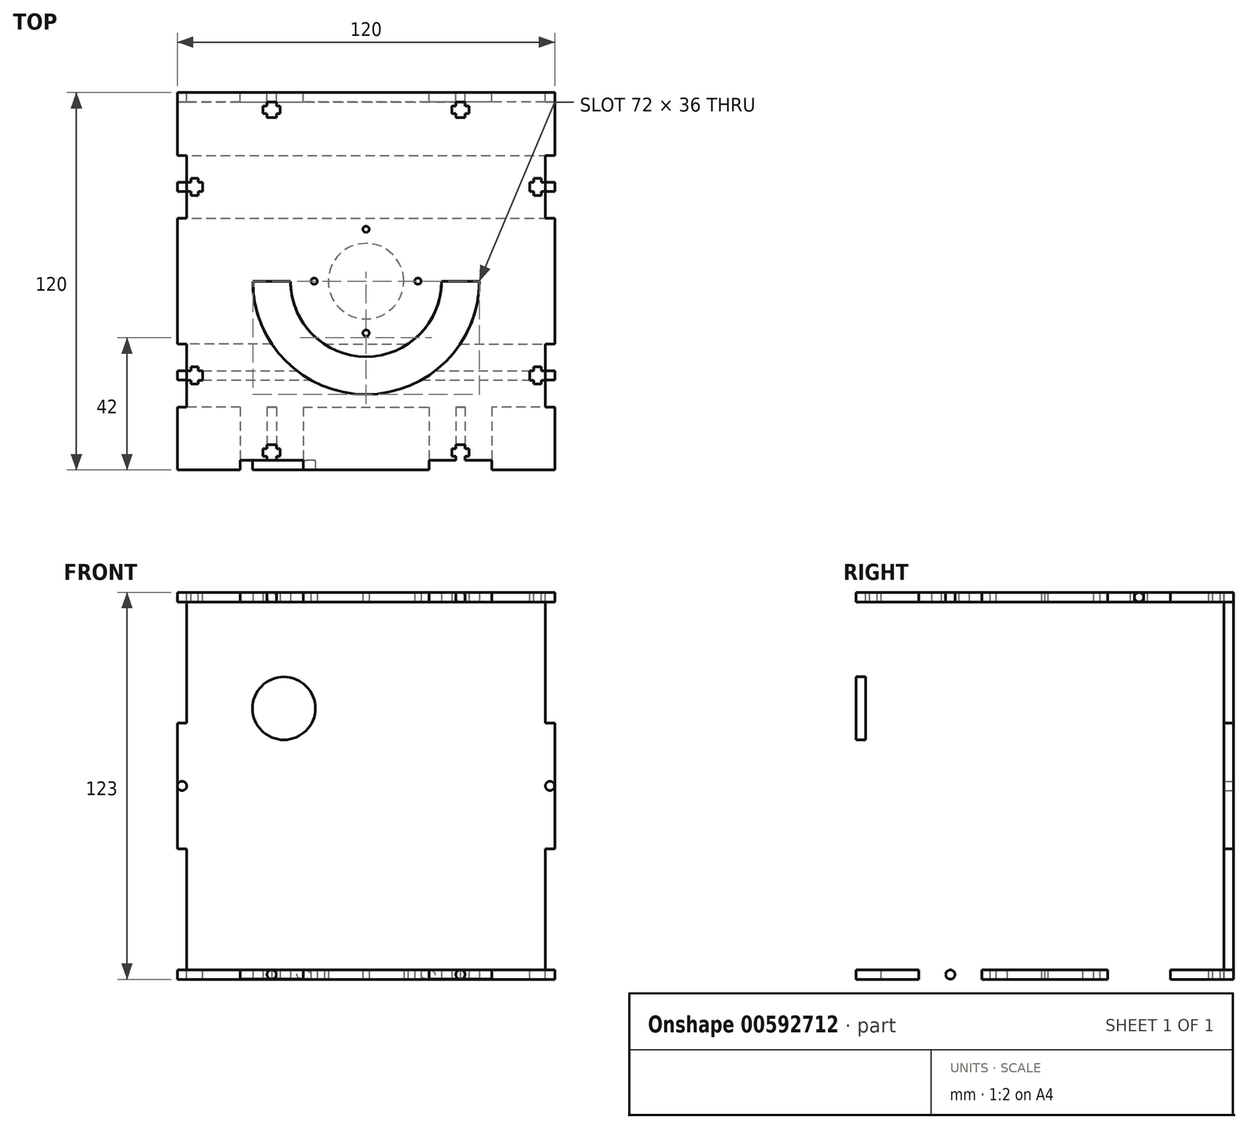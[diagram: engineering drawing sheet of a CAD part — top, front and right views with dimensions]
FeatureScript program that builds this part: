
annotation { "Feature Type Name" : "Feature", "Feature Type Description" : "" }
export const myFeature = defineFeature(function(context is Context, id is Id, definition is map)
    precondition{}
    {
        {
            var Q0;
            Q0=qCreatedBy(makeId("Top.planeOp"),FACE);
            var sketch = newSketch(context, id + "F0", { "sketchPlane" : qUnion([Q0])});
            skLineSegment(sketch, "E0.bottom", {"start": v(-60, 60) * mm, "end": v(-40, 60) * mm});
            skLineSegment(sketch, "E0.top", {"start": v(-60, -60) * mm, "end": v(-40, -60) * mm});
            skLineSegment(sketch, "E0.left", {"start": v(-60, 60) * mm, "end": v(-60, 40) * mm});
            skLineSegment(sketch, "E0.right", {"start": v(60, 60) * mm, "end": v(60, 40) * mm});
            skCircle(sketch, "E1", {"center": v(0, 0) * mm, "radius": 12 * mm});
            skCircle(sketch, "E2", {"center": v(0, -16.5) * mm, "radius": 1 * mm});
            skCircle(sketch, "E3.MirrorC", {"center": v(0, 16.5) * mm, "radius": 1 * mm});
            skLineSegment(sketch, "E4", {"start": v(57, -70.63) * mm, "end": v(57, -31.5) * mm, "construction": true});
            skLineSegment(sketch, "E5", {"start": v(-40, -57) * mm, "end": v(-40, -60) * mm});
            skLineSegment(sketch, "E6", {"start": v(-20, -57) * mm, "end": v(-20, -60) * mm});
            skLineSegment(sketch, "E7.trimOffspring", {"start": v(-20, -60) * mm, "end": v(20, -60) * mm});
            skLineSegment(sketch, "E8", {"start": v(-40, -57) * mm, "end": v(-31.5, -57) * mm});
            skLineSegment(sketch, "E9.bottom", {"start": v(-32.75, -53.3) * mm, "end": v(-31.5, -53.3) * mm});
            skLineSegment(sketch, "E9.top", {"start": v(-32.75, -55.7) * mm, "end": v(-31.5, -55.7) * mm});
            skLineSegment(sketch, "E9.left", {"start": v(-32.75, -53.3) * mm, "end": v(-32.75, -55.7) * mm});
            skLineSegment(sketch, "E9.right", {"start": v(-27.25, -53.3) * mm, "end": v(-27.25, -55.7) * mm});
            skPoint(sketch, "E9.middle", {"position": v(-30, -54.5) * mm});
            skLineSegment(sketch, "E10.top", {"start": v(-28.5, -52) * mm, "end": v(-31.5, -52) * mm});
            skLineSegment(sketch, "E10.left", {"start": v(-28.5, -57) * mm, "end": v(-28.5, -55.7) * mm});
            skLineSegment(sketch, "E10.right", {"start": v(-31.5, -57) * mm, "end": v(-31.5, -55.7) * mm});
            skLineSegment(sketch, "E11.trimOffspring", {"start": v(-28.5, -57) * mm, "end": v(-20, -57) * mm});
            skLineSegment(sketch, "E12.trimOffspring", {"start": v(-28.5, -55.7) * mm, "end": v(-27.25, -55.7) * mm});
            skLineSegment(sketch, "E13.trimOffspring", {"start": v(-28.5, -53.3) * mm, "end": v(-27.25, -53.3) * mm});
            skLineSegment(sketch, "E14.trimOffspring", {"start": v(-28.5, -53.3) * mm, "end": v(-28.5, -52) * mm});
            skPoint(sketch, "E15.orphan", {"position": v(-30, -57) * mm});
            skPoint(sketch, "E16.end.orphan", {"position": v(-30, -52) * mm});
            skLineSegment(sketch, "E17.trimOffspring", {"start": v(-31.5, -53.3) * mm, "end": v(-31.5, -52) * mm});
            skLineSegment(sketch, "E18.MirrorCS", {"start": v(20, -57) * mm, "end": v(20, -60) * mm});
            skLineSegment(sketch, "E19.MirrorCS", {"start": v(28.5, -57) * mm, "end": v(20, -57) * mm});
            skLineSegment(sketch, "E20.MirrorCS", {"start": v(28.5, -57) * mm, "end": v(28.5, -55.7) * mm});
            skLineSegment(sketch, "E21.MirrorCS", {"start": v(27.25, -53.3) * mm, "end": v(27.25, -55.7) * mm});
            skLineSegment(sketch, "E22.MirrorCS", {"start": v(28.5, -55.7) * mm, "end": v(27.25, -55.7) * mm});
            skLineSegment(sketch, "E23.MirrorCS", {"start": v(28.5, -53.3) * mm, "end": v(27.25, -53.3) * mm});
            skLineSegment(sketch, "E24.MirrorCS", {"start": v(28.5, -53.3) * mm, "end": v(28.5, -52) * mm});
            skLineSegment(sketch, "E25.MirrorCS", {"start": v(28.5, -52) * mm, "end": v(31.5, -52) * mm});
            skLineSegment(sketch, "E26.MirrorCS", {"start": v(31.5, -53.3) * mm, "end": v(31.5, -52) * mm});
            skLineSegment(sketch, "E27.MirrorCS", {"start": v(32.75, -53.3) * mm, "end": v(31.5, -53.3) * mm});
            skLineSegment(sketch, "E28.MirrorCS", {"start": v(32.75, -53.3) * mm, "end": v(32.75, -55.7) * mm});
            skLineSegment(sketch, "E29.MirrorCS", {"start": v(32.75, -55.7) * mm, "end": v(31.5, -55.7) * mm});
            skLineSegment(sketch, "E30.MirrorCS", {"start": v(31.5, -57) * mm, "end": v(31.5, -55.7) * mm});
            skLineSegment(sketch, "E31.MirrorCS", {"start": v(40, -57) * mm, "end": v(31.5, -57) * mm});
            skLineSegment(sketch, "E32.MirrorCS", {"start": v(40, -57) * mm, "end": v(40, -60) * mm});
            skLineSegment(sketch, "E33.trimOffspring", {"start": v(40, -60) * mm, "end": v(60, -60) * mm});
            skLineSegment(sketch, "E34.MirrorCS", {"start": v(-31.5, 57) * mm, "end": v(-31.5, 55.7) * mm});
            skLineSegment(sketch, "E35.MirrorCS", {"start": v(-28.5, 53.3) * mm, "end": v(-28.5, 52) * mm});
            skLineSegment(sketch, "E36.MirrorCS", {"start": v(-31.5, 53.3) * mm, "end": v(-31.5, 52) * mm});
            skLineSegment(sketch, "E37.MirrorCS", {"start": v(-28.5, 52) * mm, "end": v(-31.5, 52) * mm});
            skLineSegment(sketch, "E38.MirrorCS", {"start": v(-28.5, 57) * mm, "end": v(-28.5, 55.7) * mm});
            skLineSegment(sketch, "E39.MirrorCS", {"start": v(-28.5, 53.3) * mm, "end": v(-27.25, 53.3) * mm});
            skLineSegment(sketch, "E40.MirrorCS", {"start": v(-28.5, 55.7) * mm, "end": v(-27.25, 55.7) * mm});
            skLineSegment(sketch, "E41.MirrorCS", {"start": v(-32.75, 55.7) * mm, "end": v(-31.5, 55.7) * mm});
            skLineSegment(sketch, "E42.MirrorCS", {"start": v(-32.75, 53.3) * mm, "end": v(-31.5, 53.3) * mm});
            skPoint(sketch, "E43.MirrorP", {"position": v(-30, 54.5) * mm});
            skLineSegment(sketch, "E44.MirrorCS", {"start": v(-32.75, 53.3) * mm, "end": v(-32.75, 55.7) * mm});
            skLineSegment(sketch, "E45.MirrorCS", {"start": v(-27.25, 53.3) * mm, "end": v(-27.25, 55.7) * mm});
            skLineSegment(sketch, "E46.MirrorCS", {"start": v(-20, 57) * mm, "end": v(-20, 60) * mm});
            skLineSegment(sketch, "E47.MirrorCS", {"start": v(-40, 57) * mm, "end": v(-40, 60) * mm});
            skPoint(sketch, "E48.MirrorP", {"position": v(-30, 57) * mm});
            skLineSegment(sketch, "E49.MirrorCS", {"start": v(-28.5, 57) * mm, "end": v(-20, 57) * mm});
            skLineSegment(sketch, "E50.MirrorCS", {"start": v(-40, 57) * mm, "end": v(-31.5, 57) * mm});
            skPoint(sketch, "E51.MirrorP", {"position": v(-30, 52) * mm});
            skLineSegment(sketch, "E52.MirrorCS", {"start": v(32.75, 53.3) * mm, "end": v(31.5, 53.3) * mm});
            skLineSegment(sketch, "E53.MirrorCS", {"start": v(28.5, 53.3) * mm, "end": v(28.5, 52) * mm});
            skLineSegment(sketch, "E54.MirrorCS", {"start": v(28.5, 55.7) * mm, "end": v(27.25, 55.7) * mm});
            skLineSegment(sketch, "E55.MirrorCS", {"start": v(28.5, 57) * mm, "end": v(28.5, 55.7) * mm});
            skLineSegment(sketch, "E56.MirrorCS", {"start": v(31.5, 53.3) * mm, "end": v(31.5, 52) * mm});
            skLineSegment(sketch, "E57.MirrorCS", {"start": v(31.5, 57) * mm, "end": v(31.5, 55.7) * mm});
            skLineSegment(sketch, "E58.MirrorCS", {"start": v(28.5, 53.3) * mm, "end": v(27.25, 53.3) * mm});
            skLineSegment(sketch, "E59.MirrorCS", {"start": v(32.75, 55.7) * mm, "end": v(31.5, 55.7) * mm});
            skLineSegment(sketch, "E60.MirrorCS", {"start": v(32.75, 53.3) * mm, "end": v(32.75, 55.7) * mm});
            skLineSegment(sketch, "E61.MirrorCS", {"start": v(28.5, 52) * mm, "end": v(31.5, 52) * mm});
            skLineSegment(sketch, "E62.MirrorCS", {"start": v(40, 57) * mm, "end": v(40, 60) * mm});
            skLineSegment(sketch, "E63.MirrorCS", {"start": v(28.5, 57) * mm, "end": v(20, 57) * mm});
            skLineSegment(sketch, "E64.MirrorCS", {"start": v(40, 57) * mm, "end": v(31.5, 57) * mm});
            skLineSegment(sketch, "E65.MirrorCS", {"start": v(20, 57) * mm, "end": v(20, 60) * mm});
            skLineSegment(sketch, "E66.MirrorCS", {"start": v(27.25, 53.3) * mm, "end": v(27.25, 55.7) * mm});
            skLineSegment(sketch, "E67.trimOffspring", {"start": v(-20, 60) * mm, "end": v(20, 60) * mm});
            skLineSegment(sketch, "E68.trimOffspring", {"start": v(40, 60) * mm, "end": v(60, 60) * mm});
            skLineSegment(sketch, "E69", {"start": v(52.88, -20) * mm, "end": v(67.45, -20) * mm, "construction": true});
            skLineSegment(sketch, "E70", {"start": v(52.88, -40) * mm, "end": v(68.37, -40) * mm, "construction": true});
            skLineSegment(sketch, "E71", {"start": v(57, -40) * mm, "end": v(57, -31.5) * mm});
            skLineSegment(sketch, "E72", {"start": v(57, -20) * mm, "end": v(60, -20) * mm});
            skLineSegment(sketch, "E73", {"start": v(57, -40) * mm, "end": v(60, -40) * mm});
            skLineSegment(sketch, "E74.trimOffspring", {"start": v(60, -40) * mm, "end": v(60, -60) * mm});
            skLineSegment(sketch, "E75.bottom", {"start": v(55.7, -32.75) * mm, "end": v(53.3, -32.75) * mm});
            skLineSegment(sketch, "E75.top", {"start": v(55.7, -27.25) * mm, "end": v(53.3, -27.25) * mm});
            skLineSegment(sketch, "E75.left", {"start": v(55.7, -32.75) * mm, "end": v(55.7, -31.5) * mm});
            skLineSegment(sketch, "E75.right", {"start": v(53.3, -32.75) * mm, "end": v(53.3, -31.5) * mm});
            skPoint(sketch, "E75.middle", {"position": v(54.5, -30) * mm});
            skLineSegment(sketch, "E76.bottom", {"start": v(57, -28.5) * mm, "end": v(55.7, -28.5) * mm});
            skLineSegment(sketch, "E76.top", {"start": v(57, -31.5) * mm, "end": v(55.7, -31.5) * mm});
            skLineSegment(sketch, "E76.right", {"start": v(52, -28.5) * mm, "end": v(52, -31.5) * mm});
            skLineSegment(sketch, "E77.trimOffspring", {"start": v(57, -28.5) * mm, "end": v(57, 28.5) * mm, "construction": true});
            skLineSegment(sketch, "E78.trimOffspring", {"start": v(55.7, -28.5) * mm, "end": v(55.7, -27.25) * mm});
            skLineSegment(sketch, "E79.trimOffspring", {"start": v(53.3, -31.5) * mm, "end": v(52, -31.5) * mm});
            skLineSegment(sketch, "E80.trimOffspring", {"start": v(53.3, -28.5) * mm, "end": v(53.3, -27.25) * mm});
            skPoint(sketch, "E81.orphan", {"position": v(52, -30) * mm});
            skLineSegment(sketch, "E82.trimOffspring", {"start": v(57, -28.5) * mm, "end": v(57, -20) * mm});
            skLineSegment(sketch, "E83.trimOffspring", {"start": v(53.3, -28.5) * mm, "end": v(52, -28.5) * mm});
            skLineSegment(sketch, "E84.MirrorCS", {"start": v(57, 31.5) * mm, "end": v(55.7, 31.5) * mm});
            skLineSegment(sketch, "E85.MirrorCS", {"start": v(53.3, 31.5) * mm, "end": v(52, 31.5) * mm});
            skLineSegment(sketch, "E86.MirrorCS", {"start": v(53.3, 32.75) * mm, "end": v(53.3, 31.5) * mm});
            skLineSegment(sketch, "E87.MirrorCS", {"start": v(53.3, 28.5) * mm, "end": v(52, 28.5) * mm});
            skLineSegment(sketch, "E88.MirrorCS", {"start": v(55.7, 32.75) * mm, "end": v(53.3, 32.75) * mm});
            skLineSegment(sketch, "E89.MirrorCS", {"start": v(55.7, 28.5) * mm, "end": v(55.7, 27.25) * mm});
            skLineSegment(sketch, "E90.MirrorCS", {"start": v(55.7, 27.25) * mm, "end": v(53.3, 27.25) * mm});
            skLineSegment(sketch, "E91.MirrorCS", {"start": v(55.7, 32.75) * mm, "end": v(55.7, 31.5) * mm});
            skLineSegment(sketch, "E92.MirrorCS", {"start": v(57, 28.5) * mm, "end": v(55.7, 28.5) * mm});
            skLineSegment(sketch, "E93.MirrorCS", {"start": v(53.3, 28.5) * mm, "end": v(53.3, 27.25) * mm});
            skPoint(sketch, "E94.MirrorP", {"position": v(54.5, 30) * mm});
            skLineSegment(sketch, "E95.MirrorCS", {"start": v(52, 28.5) * mm, "end": v(52, 31.5) * mm});
            skLineSegment(sketch, "E96.MirrorCS", {"start": v(57, 20) * mm, "end": v(60, 20) * mm});
            skLineSegment(sketch, "E97.MirrorCS", {"start": v(57, 40) * mm, "end": v(60, 40) * mm});
            skPoint(sketch, "E98.MirrorP", {"position": v(52, 30) * mm});
            skLineSegment(sketch, "E99.MirrorCS", {"start": v(57, 40) * mm, "end": v(57, 31.5) * mm});
            skLineSegment(sketch, "E100.MirrorCS", {"start": v(57, 30) * mm, "end": v(57, 20) * mm});
            skLineSegment(sketch, "E101.trimOffspring", {"start": v(60, 20) * mm, "end": v(60, -20) * mm});
            skLineSegment(sketch, "E102.trimOffspring", {"start": v(57, 30) * mm, "end": v(57, 81.9) * mm, "construction": true});
            skPoint(sketch, "E103.orphan", {"position": v(53.3, -30) * mm});
            skPoint(sketch, "E104.start.orphan", {"position": v(57, -30) * mm});
            skPoint(sketch, "E105.MirrorCS.end.orphan", {"position": v(53.3, 30) * mm});
            skLineSegment(sketch, "E106.MirrorCS", {"start": v(-57, -28.5) * mm, "end": v(-55.7, -28.5) * mm});
            skLineSegment(sketch, "E107.MirrorCS", {"start": v(-57, -31.5) * mm, "end": v(-55.7, -31.5) * mm});
            skLineSegment(sketch, "E108.MirrorCS", {"start": v(-53.3, -28.5) * mm, "end": v(-52, -28.5) * mm});
            skLineSegment(sketch, "E109.MirrorCS", {"start": v(-53.3, 31.5) * mm, "end": v(-52, 31.5) * mm});
            skLineSegment(sketch, "E110.MirrorCS", {"start": v(-55.7, -32.75) * mm, "end": v(-53.3, -32.75) * mm});
            skLineSegment(sketch, "E111.MirrorCS", {"start": v(-55.7, -27.25) * mm, "end": v(-53.3, -27.25) * mm});
            skLineSegment(sketch, "E112.MirrorCS", {"start": v(-55.7, 28.5) * mm, "end": v(-55.7, 27.25) * mm});
            skLineSegment(sketch, "E113.MirrorCS", {"start": v(-53.3, -31.5) * mm, "end": v(-52, -31.5) * mm});
            skLineSegment(sketch, "E114.MirrorCS", {"start": v(-55.7, -32.75) * mm, "end": v(-55.7, -31.5) * mm});
            skLineSegment(sketch, "E115.MirrorCS", {"start": v(-53.3, -28.5) * mm, "end": v(-53.3, -27.25) * mm});
            skLineSegment(sketch, "E116.MirrorCS", {"start": v(-53.3, -32.75) * mm, "end": v(-53.3, -31.5) * mm});
            skLineSegment(sketch, "E117.MirrorCS", {"start": v(-52, -28.5) * mm, "end": v(-52, -31.5) * mm});
            skLineSegment(sketch, "E118.MirrorCS", {"start": v(-53.3, 28.5) * mm, "end": v(-53.3, 27.25) * mm});
            skLineSegment(sketch, "E119.MirrorCS", {"start": v(-57, 31.5) * mm, "end": v(-55.7, 31.5) * mm});
            skLineSegment(sketch, "E120.MirrorCS", {"start": v(-57, 28.5) * mm, "end": v(-55.7, 28.5) * mm});
            skPoint(sketch, "E121.MirrorP", {"position": v(-54.5, -30) * mm});
            skLineSegment(sketch, "E122.MirrorCS", {"start": v(-52, 28.5) * mm, "end": v(-52, 31.5) * mm});
            skLineSegment(sketch, "E123.MirrorCS", {"start": v(-53.3, 28.5) * mm, "end": v(-52, 28.5) * mm});
            skLineSegment(sketch, "E124.MirrorCS", {"start": v(-55.7, -28.5) * mm, "end": v(-55.7, -27.25) * mm});
            skPoint(sketch, "E125.MirrorP", {"position": v(-54.5, 30) * mm});
            skLineSegment(sketch, "E126.MirrorCS", {"start": v(-53.3, 32.75) * mm, "end": v(-53.3, 31.5) * mm});
            skPoint(sketch, "E127.MirrorP", {"position": v(-53.3, 30) * mm});
            skLineSegment(sketch, "E128.MirrorCS", {"start": v(-57, -40) * mm, "end": v(-60, -40) * mm});
            skLineSegment(sketch, "E129.MirrorCS", {"start": v(-57, -20) * mm, "end": v(-60, -20) * mm});
            skLineSegment(sketch, "E130.MirrorCS", {"start": v(-57, 20) * mm, "end": v(-60, 20) * mm});
            skLineSegment(sketch, "E131.MirrorCS", {"start": v(-55.7, 32.75) * mm, "end": v(-53.3, 32.75) * mm});
            skLineSegment(sketch, "E132.MirrorCS", {"start": v(-57, 40) * mm, "end": v(-60, 40) * mm});
            skLineSegment(sketch, "E133.MirrorCS", {"start": v(-55.7, 27.25) * mm, "end": v(-53.3, 27.25) * mm});
            skPoint(sketch, "E134.MirrorP", {"position": v(-53.3, -30) * mm});
            skLineSegment(sketch, "E135.MirrorCS", {"start": v(-55.7, 32.75) * mm, "end": v(-55.7, 31.5) * mm});
            skLineSegment(sketch, "E136.MirrorCS", {"start": v(-57, 30) * mm, "end": v(-57, 20) * mm});
            skLineSegment(sketch, "E137.MirrorCS", {"start": v(-57, -28.5) * mm, "end": v(-57, -20) * mm});
            skLineSegment(sketch, "E138.MirrorCS", {"start": v(-57, -28.5) * mm, "end": v(-57, 28.5) * mm, "construction": true});
            skPoint(sketch, "E139.MirrorP", {"position": v(-52, -30) * mm});
            skPoint(sketch, "E140.MirrorP", {"position": v(-57, -30) * mm});
            skLineSegment(sketch, "E141.MirrorCS", {"start": v(-57, 40) * mm, "end": v(-57, 31.5) * mm});
            skPoint(sketch, "E142.MirrorP", {"position": v(-52, 30) * mm});
            skLineSegment(sketch, "E143.MirrorCS", {"start": v(-57, -40) * mm, "end": v(-57, -31.5) * mm});
            skLineSegment(sketch, "E144.MirrorCS", {"start": v(-60, 20) * mm, "end": v(-60, -20) * mm});
            skLineSegment(sketch, "E145.trimOffspring", {"start": v(-60, -40) * mm, "end": v(-60, -60) * mm});
            skCircle(sketch, "E146", {"center": v(16.5, 0) * mm, "radius": 1 * mm});
            skCircle(sketch, "E147", {"center": v(-16.5, 0) * mm, "radius": 1 * mm});
            skArc(sketch, "E148", {"start": v(24, 0) * mm, "mid": v(0, -24) * mm, "end": v(-24, 0) * mm});
            skArc(sketch, "E149", {"start": v(36, 0) * mm, "mid": v(0, -36) * mm, "end": v(-36, 0) * mm});
            skLineSegment(sketch, "E150", {"start": v(-36, 0) * mm, "end": v(-24, 0) * mm});
            skLineSegment(sketch, "E151", {"start": v(24, 0) * mm, "end": v(36, 0) * mm});
            skSolve(sketch);
        }
        {
            var Q0;
            Q0=makeQuery(id+"F0.imprint","IMPRINT",FACE,{"disambiguationData":[TD([[makeQuery(id+"F0.imprint","IMPRINT",EDGE,{"derivedFrom":sQuery(id+"F0.wireOp",EDGE,"E0.bottom")}),-1.0]])]});
            extrude(context, id + "F1", {"entities" : qUnion([Q0]), "depth" : 3 * mm, "offsetDistance" : 25 * mm});
        }
        {
            var Q0;
            Q0=makeQuery(id+"F1.opExtrude","SWEPT_BODY",BODY,{"disambiguationData":[OSD([sQuery(id+"F0.wireOp",EDGE,"E0.bottom"),sQuery(id+"F0.wireOp",EDGE,"E0.top"),sQuery(id+"F0.wireOp",EDGE,"E0.left"),sQuery(id+"F0.wireOp",EDGE,"E0.right"),sQuery(id+"F0.wireOp",EDGE,"E1"),sQuery(id+"F0.wireOp",EDGE,"E2"),sQuery(id+"F0.wireOp",EDGE,"E3.MirrorC"),sQuery(id+"F0.wireOp",EDGE,"E5"),sQuery(id+"F0.wireOp",EDGE,"E6"),sQuery(id+"F0.wireOp",EDGE,"E7.trimOffspring"),sQuery(id+"F0.wireOp",EDGE,"E8"),sQuery(id+"F0.wireOp",EDGE,"E9.bottom"),sQuery(id+"F0.wireOp",EDGE,"E9.top"),sQuery(id+"F0.wireOp",EDGE,"E9.left"),sQuery(id+"F0.wireOp",EDGE,"E9.right"),sQuery(id+"F0.wireOp",EDGE,"E10.top"),sQuery(id+"F0.wireOp",EDGE,"E10.left"),sQuery(id+"F0.wireOp",EDGE,"E10.right"),sQuery(id+"F0.wireOp",EDGE,"E11.trimOffspring"),sQuery(id+"F0.wireOp",EDGE,"E12.trimOffspring"),sQuery(id+"F0.wireOp",EDGE,"E13.trimOffspring"),sQuery(id+"F0.wireOp",EDGE,"E14.trimOffspring"),sQuery(id+"F0.wireOp",EDGE,"E17.trimOffspring"),sQuery(id+"F0.wireOp",EDGE,"E18.MirrorCS"),sQuery(id+"F0.wireOp",EDGE,"E19.MirrorCS"),sQuery(id+"F0.wireOp",EDGE,"E20.MirrorCS"),sQuery(id+"F0.wireOp",EDGE,"E21.MirrorCS"),sQuery(id+"F0.wireOp",EDGE,"E22.MirrorCS"),sQuery(id+"F0.wireOp",EDGE,"E23.MirrorCS"),sQuery(id+"F0.wireOp",EDGE,"E24.MirrorCS"),sQuery(id+"F0.wireOp",EDGE,"E25.MirrorCS"),sQuery(id+"F0.wireOp",EDGE,"E26.MirrorCS"),sQuery(id+"F0.wireOp",EDGE,"E27.MirrorCS"),sQuery(id+"F0.wireOp",EDGE,"E28.MirrorCS"),sQuery(id+"F0.wireOp",EDGE,"E29.MirrorCS"),sQuery(id+"F0.wireOp",EDGE,"E30.MirrorCS"),sQuery(id+"F0.wireOp",EDGE,"E31.MirrorCS"),sQuery(id+"F0.wireOp",EDGE,"E32.MirrorCS"),sQuery(id+"F0.wireOp",EDGE,"E33.trimOffspring"),sQuery(id+"F0.wireOp",EDGE,"E34.MirrorCS"),sQuery(id+"F0.wireOp",EDGE,"E35.MirrorCS"),sQuery(id+"F0.wireOp",EDGE,"E36.MirrorCS"),sQuery(id+"F0.wireOp",EDGE,"E37.MirrorCS"),sQuery(id+"F0.wireOp",EDGE,"E38.MirrorCS"),sQuery(id+"F0.wireOp",EDGE,"E39.MirrorCS"),sQuery(id+"F0.wireOp",EDGE,"E40.MirrorCS"),sQuery(id+"F0.wireOp",EDGE,"E41.MirrorCS"),sQuery(id+"F0.wireOp",EDGE,"E42.MirrorCS"),sQuery(id+"F0.wireOp",EDGE,"E44.MirrorCS"),sQuery(id+"F0.wireOp",EDGE,"E45.MirrorCS"),sQuery(id+"F0.wireOp",EDGE,"E46.MirrorCS"),sQuery(id+"F0.wireOp",EDGE,"E47.MirrorCS"),sQuery(id+"F0.wireOp",EDGE,"E49.MirrorCS"),sQuery(id+"F0.wireOp",EDGE,"E50.MirrorCS"),sQuery(id+"F0.wireOp",EDGE,"E52.MirrorCS"),sQuery(id+"F0.wireOp",EDGE,"E53.MirrorCS"),sQuery(id+"F0.wireOp",EDGE,"E54.MirrorCS"),sQuery(id+"F0.wireOp",EDGE,"E55.MirrorCS"),sQuery(id+"F0.wireOp",EDGE,"E56.MirrorCS"),sQuery(id+"F0.wireOp",EDGE,"E57.MirrorCS"),sQuery(id+"F0.wireOp",EDGE,"E58.MirrorCS"),sQuery(id+"F0.wireOp",EDGE,"E59.MirrorCS"),sQuery(id+"F0.wireOp",EDGE,"E60.MirrorCS"),sQuery(id+"F0.wireOp",EDGE,"E61.MirrorCS"),sQuery(id+"F0.wireOp",EDGE,"E62.MirrorCS"),sQuery(id+"F0.wireOp",EDGE,"E63.MirrorCS"),sQuery(id+"F0.wireOp",EDGE,"E64.MirrorCS"),sQuery(id+"F0.wireOp",EDGE,"E65.MirrorCS"),sQuery(id+"F0.wireOp",EDGE,"E66.MirrorCS"),sQuery(id+"F0.wireOp",EDGE,"E67.trimOffspring"),sQuery(id+"F0.wireOp",EDGE,"E68.trimOffspring"),sQuery(id+"F0.wireOp",EDGE,"E71"),sQuery(id+"F0.wireOp",EDGE,"E72"),sQuery(id+"F0.wireOp",EDGE,"E73"),sQuery(id+"F0.wireOp",EDGE,"E74.trimOffspring"),sQuery(id+"F0.wireOp",EDGE,"E75.bottom"),sQuery(id+"F0.wireOp",EDGE,"E75.top"),sQuery(id+"F0.wireOp",EDGE,"E75.left"),sQuery(id+"F0.wireOp",EDGE,"E75.right"),sQuery(id+"F0.wireOp",EDGE,"E76.bottom"),sQuery(id+"F0.wireOp",EDGE,"E76.top"),sQuery(id+"F0.wireOp",EDGE,"E76.right"),sQuery(id+"F0.wireOp",EDGE,"E78.trimOffspring"),sQuery(id+"F0.wireOp",EDGE,"E79.trimOffspring"),sQuery(id+"F0.wireOp",EDGE,"E80.trimOffspring"),sQuery(id+"F0.wireOp",EDGE,"E82.trimOffspring"),sQuery(id+"F0.wireOp",EDGE,"E83.trimOffspring"),sQuery(id+"F0.wireOp",EDGE,"E84.MirrorCS"),sQuery(id+"F0.wireOp",EDGE,"E85.MirrorCS"),sQuery(id+"F0.wireOp",EDGE,"E86.MirrorCS"),sQuery(id+"F0.wireOp",EDGE,"E87.MirrorCS"),sQuery(id+"F0.wireOp",EDGE,"E88.MirrorCS"),sQuery(id+"F0.wireOp",EDGE,"E89.MirrorCS"),sQuery(id+"F0.wireOp",EDGE,"E90.MirrorCS"),sQuery(id+"F0.wireOp",EDGE,"E91.MirrorCS"),sQuery(id+"F0.wireOp",EDGE,"E92.MirrorCS"),sQuery(id+"F0.wireOp",EDGE,"E93.MirrorCS"),sQuery(id+"F0.wireOp",EDGE,"E95.MirrorCS"),sQuery(id+"F0.wireOp",EDGE,"E96.MirrorCS"),sQuery(id+"F0.wireOp",EDGE,"E97.MirrorCS"),sQuery(id+"F0.wireOp",EDGE,"E99.MirrorCS"),sQuery(id+"F0.wireOp",EDGE,"E100.MirrorCS"),sQuery(id+"F0.wireOp",EDGE,"E101.trimOffspring"),sQuery(id+"F0.wireOp",EDGE,"E106.MirrorCS"),sQuery(id+"F0.wireOp",EDGE,"E107.MirrorCS"),sQuery(id+"F0.wireOp",EDGE,"E108.MirrorCS"),sQuery(id+"F0.wireOp",EDGE,"E109.MirrorCS"),sQuery(id+"F0.wireOp",EDGE,"E110.MirrorCS"),sQuery(id+"F0.wireOp",EDGE,"E111.MirrorCS"),sQuery(id+"F0.wireOp",EDGE,"E112.MirrorCS"),sQuery(id+"F0.wireOp",EDGE,"E113.MirrorCS"),sQuery(id+"F0.wireOp",EDGE,"E114.MirrorCS"),sQuery(id+"F0.wireOp",EDGE,"E115.MirrorCS"),sQuery(id+"F0.wireOp",EDGE,"E116.MirrorCS"),sQuery(id+"F0.wireOp",EDGE,"E117.MirrorCS"),sQuery(id+"F0.wireOp",EDGE,"E118.MirrorCS"),sQuery(id+"F0.wireOp",EDGE,"E119.MirrorCS"),sQuery(id+"F0.wireOp",EDGE,"E120.MirrorCS"),sQuery(id+"F0.wireOp",EDGE,"E122.MirrorCS"),sQuery(id+"F0.wireOp",EDGE,"E123.MirrorCS"),sQuery(id+"F0.wireOp",EDGE,"E124.MirrorCS"),sQuery(id+"F0.wireOp",EDGE,"E126.MirrorCS"),sQuery(id+"F0.wireOp",EDGE,"E128.MirrorCS"),sQuery(id+"F0.wireOp",EDGE,"E129.MirrorCS"),sQuery(id+"F0.wireOp",EDGE,"E130.MirrorCS"),sQuery(id+"F0.wireOp",EDGE,"E131.MirrorCS"),sQuery(id+"F0.wireOp",EDGE,"E132.MirrorCS"),sQuery(id+"F0.wireOp",EDGE,"E133.MirrorCS"),sQuery(id+"F0.wireOp",EDGE,"E135.MirrorCS"),sQuery(id+"F0.wireOp",EDGE,"E136.MirrorCS"),sQuery(id+"F0.wireOp",EDGE,"E137.MirrorCS"),sQuery(id+"F0.wireOp",EDGE,"E141.MirrorCS"),sQuery(id+"F0.wireOp",EDGE,"E143.MirrorCS"),sQuery(id+"F0.wireOp",EDGE,"E145.trimOffspring"),sQuery(id+"F0.wireOp",EDGE,"E144.MirrorCS")])]});
            transform(context, id + "F2", {"entities" : qUnion([Q0]), "transformType" : TransformType.TRANSLATION_3D, "dx" : 0 * mm, "dy" : 0 * mm, "dz" : 120 * mm, "makeCopy" : true});
        }
        {
            var Q0;
            Q0=makeQuery(id+"F2.opPattern","COPY",FACE,{"derivedFrom":makeQuery(id+"F1.opExtrude","CAP_FACE",FACE,{"disambiguationData":[OSD([sQuery(id+"F0.wireOp",EDGE,"E0.bottom"),sQuery(id+"F0.wireOp",EDGE,"E0.top"),sQuery(id+"F0.wireOp",EDGE,"E0.left"),sQuery(id+"F0.wireOp",EDGE,"E0.right"),sQuery(id+"F0.wireOp",EDGE,"E1"),sQuery(id+"F0.wireOp",EDGE,"E2"),sQuery(id+"F0.wireOp",EDGE,"E3.MirrorC"),sQuery(id+"F0.wireOp",EDGE,"E5"),sQuery(id+"F0.wireOp",EDGE,"E6"),sQuery(id+"F0.wireOp",EDGE,"E7.trimOffspring"),sQuery(id+"F0.wireOp",EDGE,"E8"),sQuery(id+"F0.wireOp",EDGE,"E9.bottom"),sQuery(id+"F0.wireOp",EDGE,"E9.top"),sQuery(id+"F0.wireOp",EDGE,"E9.left"),sQuery(id+"F0.wireOp",EDGE,"E9.right"),sQuery(id+"F0.wireOp",EDGE,"E10.top"),sQuery(id+"F0.wireOp",EDGE,"E10.left"),sQuery(id+"F0.wireOp",EDGE,"E10.right"),sQuery(id+"F0.wireOp",EDGE,"E11.trimOffspring"),sQuery(id+"F0.wireOp",EDGE,"E12.trimOffspring"),sQuery(id+"F0.wireOp",EDGE,"E13.trimOffspring"),sQuery(id+"F0.wireOp",EDGE,"E14.trimOffspring"),sQuery(id+"F0.wireOp",EDGE,"E17.trimOffspring"),sQuery(id+"F0.wireOp",EDGE,"E18.MirrorCS"),sQuery(id+"F0.wireOp",EDGE,"E19.MirrorCS"),sQuery(id+"F0.wireOp",EDGE,"E20.MirrorCS"),sQuery(id+"F0.wireOp",EDGE,"E21.MirrorCS"),sQuery(id+"F0.wireOp",EDGE,"E22.MirrorCS"),sQuery(id+"F0.wireOp",EDGE,"E23.MirrorCS"),sQuery(id+"F0.wireOp",EDGE,"E24.MirrorCS"),sQuery(id+"F0.wireOp",EDGE,"E25.MirrorCS"),sQuery(id+"F0.wireOp",EDGE,"E26.MirrorCS"),sQuery(id+"F0.wireOp",EDGE,"E27.MirrorCS"),sQuery(id+"F0.wireOp",EDGE,"E28.MirrorCS"),sQuery(id+"F0.wireOp",EDGE,"E29.MirrorCS"),sQuery(id+"F0.wireOp",EDGE,"E30.MirrorCS"),sQuery(id+"F0.wireOp",EDGE,"E31.MirrorCS"),sQuery(id+"F0.wireOp",EDGE,"E32.MirrorCS"),sQuery(id+"F0.wireOp",EDGE,"E33.trimOffspring"),sQuery(id+"F0.wireOp",EDGE,"E34.MirrorCS"),sQuery(id+"F0.wireOp",EDGE,"E35.MirrorCS"),sQuery(id+"F0.wireOp",EDGE,"E36.MirrorCS"),sQuery(id+"F0.wireOp",EDGE,"E37.MirrorCS"),sQuery(id+"F0.wireOp",EDGE,"E38.MirrorCS"),sQuery(id+"F0.wireOp",EDGE,"E39.MirrorCS"),sQuery(id+"F0.wireOp",EDGE,"E40.MirrorCS"),sQuery(id+"F0.wireOp",EDGE,"E41.MirrorCS"),sQuery(id+"F0.wireOp",EDGE,"E42.MirrorCS"),sQuery(id+"F0.wireOp",EDGE,"E44.MirrorCS"),sQuery(id+"F0.wireOp",EDGE,"E45.MirrorCS"),sQuery(id+"F0.wireOp",EDGE,"E46.MirrorCS"),sQuery(id+"F0.wireOp",EDGE,"E47.MirrorCS"),sQuery(id+"F0.wireOp",EDGE,"E49.MirrorCS"),sQuery(id+"F0.wireOp",EDGE,"E50.MirrorCS"),sQuery(id+"F0.wireOp",EDGE,"E52.MirrorCS"),sQuery(id+"F0.wireOp",EDGE,"E53.MirrorCS"),sQuery(id+"F0.wireOp",EDGE,"E54.MirrorCS"),sQuery(id+"F0.wireOp",EDGE,"E55.MirrorCS"),sQuery(id+"F0.wireOp",EDGE,"E56.MirrorCS"),sQuery(id+"F0.wireOp",EDGE,"E57.MirrorCS"),sQuery(id+"F0.wireOp",EDGE,"E58.MirrorCS"),sQuery(id+"F0.wireOp",EDGE,"E59.MirrorCS"),sQuery(id+"F0.wireOp",EDGE,"E60.MirrorCS"),sQuery(id+"F0.wireOp",EDGE,"E61.MirrorCS"),sQuery(id+"F0.wireOp",EDGE,"E62.MirrorCS"),sQuery(id+"F0.wireOp",EDGE,"E63.MirrorCS"),sQuery(id+"F0.wireOp",EDGE,"E64.MirrorCS"),sQuery(id+"F0.wireOp",EDGE,"E65.MirrorCS"),sQuery(id+"F0.wireOp",EDGE,"E66.MirrorCS"),sQuery(id+"F0.wireOp",EDGE,"E67.trimOffspring"),sQuery(id+"F0.wireOp",EDGE,"E68.trimOffspring"),sQuery(id+"F0.wireOp",EDGE,"E71"),sQuery(id+"F0.wireOp",EDGE,"E72"),sQuery(id+"F0.wireOp",EDGE,"E73"),sQuery(id+"F0.wireOp",EDGE,"E74.trimOffspring"),sQuery(id+"F0.wireOp",EDGE,"E75.bottom"),sQuery(id+"F0.wireOp",EDGE,"E75.top"),sQuery(id+"F0.wireOp",EDGE,"E75.left"),sQuery(id+"F0.wireOp",EDGE,"E75.right"),sQuery(id+"F0.wireOp",EDGE,"E76.bottom"),sQuery(id+"F0.wireOp",EDGE,"E76.top"),sQuery(id+"F0.wireOp",EDGE,"E76.right"),sQuery(id+"F0.wireOp",EDGE,"E78.trimOffspring"),sQuery(id+"F0.wireOp",EDGE,"E79.trimOffspring"),sQuery(id+"F0.wireOp",EDGE,"E80.trimOffspring"),sQuery(id+"F0.wireOp",EDGE,"E82.trimOffspring"),sQuery(id+"F0.wireOp",EDGE,"E83.trimOffspring"),sQuery(id+"F0.wireOp",EDGE,"E84.MirrorCS"),sQuery(id+"F0.wireOp",EDGE,"E85.MirrorCS"),sQuery(id+"F0.wireOp",EDGE,"E86.MirrorCS"),sQuery(id+"F0.wireOp",EDGE,"E87.MirrorCS"),sQuery(id+"F0.wireOp",EDGE,"E88.MirrorCS"),sQuery(id+"F0.wireOp",EDGE,"E89.MirrorCS"),sQuery(id+"F0.wireOp",EDGE,"E90.MirrorCS"),sQuery(id+"F0.wireOp",EDGE,"E91.MirrorCS"),sQuery(id+"F0.wireOp",EDGE,"E92.MirrorCS"),sQuery(id+"F0.wireOp",EDGE,"E93.MirrorCS"),sQuery(id+"F0.wireOp",EDGE,"E95.MirrorCS"),sQuery(id+"F0.wireOp",EDGE,"E96.MirrorCS"),sQuery(id+"F0.wireOp",EDGE,"E97.MirrorCS"),sQuery(id+"F0.wireOp",EDGE,"E99.MirrorCS"),sQuery(id+"F0.wireOp",EDGE,"E100.MirrorCS"),sQuery(id+"F0.wireOp",EDGE,"E101.trimOffspring"),sQuery(id+"F0.wireOp",EDGE,"E106.MirrorCS"),sQuery(id+"F0.wireOp",EDGE,"E107.MirrorCS"),sQuery(id+"F0.wireOp",EDGE,"E108.MirrorCS"),sQuery(id+"F0.wireOp",EDGE,"E109.MirrorCS"),sQuery(id+"F0.wireOp",EDGE,"E110.MirrorCS"),sQuery(id+"F0.wireOp",EDGE,"E111.MirrorCS"),sQuery(id+"F0.wireOp",EDGE,"E112.MirrorCS"),sQuery(id+"F0.wireOp",EDGE,"E113.MirrorCS"),sQuery(id+"F0.wireOp",EDGE,"E114.MirrorCS"),sQuery(id+"F0.wireOp",EDGE,"E115.MirrorCS"),sQuery(id+"F0.wireOp",EDGE,"E116.MirrorCS"),sQuery(id+"F0.wireOp",EDGE,"E117.MirrorCS"),sQuery(id+"F0.wireOp",EDGE,"E118.MirrorCS"),sQuery(id+"F0.wireOp",EDGE,"E119.MirrorCS"),sQuery(id+"F0.wireOp",EDGE,"E120.MirrorCS"),sQuery(id+"F0.wireOp",EDGE,"E122.MirrorCS"),sQuery(id+"F0.wireOp",EDGE,"E123.MirrorCS"),sQuery(id+"F0.wireOp",EDGE,"E124.MirrorCS"),sQuery(id+"F0.wireOp",EDGE,"E126.MirrorCS"),sQuery(id+"F0.wireOp",EDGE,"E128.MirrorCS"),sQuery(id+"F0.wireOp",EDGE,"E129.MirrorCS"),sQuery(id+"F0.wireOp",EDGE,"E130.MirrorCS"),sQuery(id+"F0.wireOp",EDGE,"E131.MirrorCS"),sQuery(id+"F0.wireOp",EDGE,"E132.MirrorCS"),sQuery(id+"F0.wireOp",EDGE,"E133.MirrorCS"),sQuery(id+"F0.wireOp",EDGE,"E135.MirrorCS"),sQuery(id+"F0.wireOp",EDGE,"E136.MirrorCS"),sQuery(id+"F0.wireOp",EDGE,"E137.MirrorCS"),sQuery(id+"F0.wireOp",EDGE,"E141.MirrorCS"),sQuery(id+"F0.wireOp",EDGE,"E143.MirrorCS"),sQuery(id+"F0.wireOp",EDGE,"E145.trimOffspring"),sQuery(id+"F0.wireOp",EDGE,"E144.MirrorCS")])],"isStart":false}),"instanceName":"1"});
            var sketch = newSketch(context, id + "F3", { "sketchPlane" : qUnion([Q0])});
            skCircle(sketch, "E152", {"center": v(0, 0) * mm, "radius": 12 * mm});
            skSolve(sketch);
        }
        {
            var Q0;
            Q0=makeQuery(id+"F3.imprint","IMPRINT",FACE,{"disambiguationData":[TD([[makeQuery(id+"F3.imprint","IMPRINT",EDGE,{"derivedFrom":sQuery(id+"F3.wireOp",EDGE,"E152")}),1.0]])]});
            extrude(context, id + "F4", {"entities" : qUnion([Q0]), "operationType" : NewBodyOperationType.ADD, "oppositeDirection" : true, "depth" : 3 * mm, "offsetDistance" : 25 * mm});
        }
        {
            var Q0;
            Q0=qCreatedBy(makeId("Right.planeOp"),FACE);
            cPlane(context, id + "F5", {"entities" : qUnion([Q0]), "cplaneType" : CPlaneType.OFFSET, "offset" : 60 * mm, "width" : 150 * mm, "height" : 150 * mm});
        }
        {
            var Q0;
            Q0=qCreatedBy(id+"F5.planeOp",FACE);
            var sketch = newSketch(context, id + "F6", { "sketchPlane" : qUnion([Q0])});
            skLineSegment(sketch, "E153", {"start": v(-58.76, 3) * mm, "end": v(-40, 3) * mm, "construction": true});
            skLineSegment(sketch, "E154", {"start": v(-93.34, 120) * mm, "end": v(-40, 120) * mm, "construction": true});
            skLineSegment(sketch, "E155", {"start": v(0, 3) * mm, "end": v(0, 120) * mm, "construction": true});
            skLineSegment(sketch, "E156", {"start": v(60, -38.6) * mm, "end": v(-60, -38.6) * mm, "construction": true});
            skLineSegment(sketch, "E157", {"start": v(-60, -38.6) * mm, "end": v(-60, 41.5) * mm, "construction": true});
            skLineSegment(sketch, "E158.bottom", {"start": v(-60, 120) * mm, "end": v(-40, 120) * mm});
            skLineSegment(sketch, "E158.top", {"start": v(-60, 3) * mm, "end": v(-40, 3) * mm});
            skLineSegment(sketch, "E158.left", {"start": v(-60, 120) * mm, "end": v(-60, 81.5) * mm});
            skLineSegment(sketch, "E158.right", {"start": v(60, 120) * mm, "end": v(60, 81.5) * mm});
            skLineSegment(sketch, "E159", {"start": v(20, 7.54) * mm, "end": v(20, -10.26) * mm, "construction": true});
            skLineSegment(sketch, "E160", {"start": v(20, -10.26) * mm, "end": v(40, -10.26) * mm, "construction": true});
            skLineSegment(sketch, "E161", {"start": v(40, -10.26) * mm, "end": v(40, 9.74) * mm, "construction": true});
            skLineSegment(sketch, "E162.top", {"start": v(20, 0) * mm, "end": v(40, 0) * mm});
            skLineSegment(sketch, "E162.left", {"start": v(20, 3) * mm, "end": v(20, 0) * mm});
            skLineSegment(sketch, "E162.right", {"start": v(40, 3) * mm, "end": v(40, 0) * mm});
            skLineSegment(sketch, "E163.trimOffspring", {"start": v(40, 3) * mm, "end": v(85.78, 3) * mm, "construction": true});
            skLineSegment(sketch, "E164.trimOffspring", {"start": v(40, 3) * mm, "end": v(60, 3) * mm});
            skLineSegment(sketch, "E165", {"start": v(30, 0) * mm, "end": v(30, 3) * mm, "construction": true});
            skLineSegment(sketch, "E166.MirrorCS", {"start": v(-20, 0) * mm, "end": v(-40, 0) * mm});
            skLineSegment(sketch, "E167.MirrorCS", {"start": v(-40, 3) * mm, "end": v(-40, 0) * mm});
            skLineSegment(sketch, "E168.MirrorCS", {"start": v(-20, 3) * mm, "end": v(-20, 0) * mm});
            skLineSegment(sketch, "E169.MirrorCS", {"start": v(-20, 123) * mm, "end": v(-40, 123) * mm});
            skLineSegment(sketch, "E170.MirrorCS", {"start": v(-20, 120) * mm, "end": v(-20, 123) * mm});
            skLineSegment(sketch, "E171.MirrorCS", {"start": v(-40, 120) * mm, "end": v(-40, 123) * mm});
            skLineSegment(sketch, "E172.MirrorCS", {"start": v(20, 120) * mm, "end": v(20, 123) * mm});
            skLineSegment(sketch, "E173.MirrorCS", {"start": v(40, 120) * mm, "end": v(40, 123) * mm});
            skLineSegment(sketch, "E174.MirrorCS", {"start": v(20, 123) * mm, "end": v(40, 123) * mm});
            skPoint(sketch, "E175.orphan", {"position": v(30, 120) * mm});
            skPoint(sketch, "E176.MirrorCS.start.orphan", {"position": v(30, 123) * mm});
            skLineSegment(sketch, "E177.trimOffspring", {"start": v(40, 120) * mm, "end": v(123.57, 120) * mm, "construction": true});
            skLineSegment(sketch, "E178.trimOffspring", {"start": v(-20, 3) * mm, "end": v(20, 3) * mm, "construction": true});
            skLineSegment(sketch, "E179.trimOffspring", {"start": v(-20, 3) * mm, "end": v(20, 3) * mm});
            skPoint(sketch, "E180.orphan", {"position": v(-30, 3) * mm});
            skPoint(sketch, "E181.MirrorCS.start.orphan", {"position": v(-30, 0) * mm});
            skLineSegment(sketch, "E182.trimOffspring", {"start": v(-20, 120) * mm, "end": v(20, 120) * mm, "construction": true});
            skLineSegment(sketch, "E183.trimOffspring", {"start": v(-20, 120) * mm, "end": v(20, 120) * mm});
            skPoint(sketch, "E184.MirrorCS.start.orphan", {"position": v(-30, 123) * mm});
            skPoint(sketch, "E185.orphan", {"position": v(-30, 120) * mm});
            skLineSegment(sketch, "E186.trimOffspring", {"start": v(40, 120) * mm, "end": v(60, 120) * mm});
            skLineSegment(sketch, "E187", {"start": v(57, 139.48) * mm, "end": v(57, 62.59) * mm, "construction": true});
            skLineSegment(sketch, "E188", {"start": v(-57, 133.79) * mm, "end": v(-57, 62.59) * mm, "construction": true});
            skLineSegment(sketch, "E189", {"start": v(60, 81.5) * mm, "end": v(57, 81.5) * mm});
            skLineSegment(sketch, "E190", {"start": v(57, 81.5) * mm, "end": v(57, 62.59) * mm});
            skLineSegment(sketch, "E191", {"start": v(57, 41.5) * mm, "end": v(60, 41.5) * mm});
            skLineSegment(sketch, "E192.trimOffspring", {"start": v(60, 41.5) * mm, "end": v(60, 3) * mm});
            skLineSegment(sketch, "E193.MirrorCS", {"start": v(-57, 41.5) * mm, "end": v(-60, 41.5) * mm});
            skLineSegment(sketch, "E194.MirrorCS", {"start": v(-57, 81.5) * mm, "end": v(-57, 62.59) * mm});
            skLineSegment(sketch, "E195.MirrorCS", {"start": v(-60, 81.5) * mm, "end": v(-57, 81.5) * mm});
            skLineSegment(sketch, "E196.trimOffspring", {"start": v(-60, 81.5) * mm, "end": v(-60, 139.44) * mm, "construction": true});
            skLineSegment(sketch, "E197.trimOffspring", {"start": v(-60, 41.5) * mm, "end": v(-60, 3) * mm});
            skLineSegment(sketch, "E198.bottom", {"start": v(55.7, 64.25) * mm, "end": v(53.3, 64.25) * mm});
            skLineSegment(sketch, "E198.top", {"start": v(55.7, 58.75) * mm, "end": v(53.3, 58.75) * mm});
            skLineSegment(sketch, "E198.left", {"start": v(55.7, 64.25) * mm, "end": v(55.7, 62.59) * mm});
            skLineSegment(sketch, "E198.right", {"start": v(53.3, 64.25) * mm, "end": v(53.3, 62.59) * mm});
            skPoint(sketch, "E198.middle", {"position": v(54.5, 61.5) * mm});
            skLineSegment(sketch, "E199.bottom", {"start": v(52, 62.59) * mm, "end": v(53.3, 62.59) * mm});
            skLineSegment(sketch, "E199.top", {"start": v(52, 60.41) * mm, "end": v(53.3, 60.41) * mm});
            skLineSegment(sketch, "E199.left", {"start": v(52, 62.59) * mm, "end": v(52, 60.41) * mm});
            skLineSegment(sketch, "E200.trimOffspring", {"start": v(55.7, 60.41) * mm, "end": v(55.7, 58.75) * mm});
            skLineSegment(sketch, "E201.trimOffspring", {"start": v(55.7, 60.41) * mm, "end": v(57, 60.41) * mm});
            skLineSegment(sketch, "E202.trimOffspring", {"start": v(57, 60.41) * mm, "end": v(57, -14.3) * mm, "construction": true});
            skLineSegment(sketch, "E203.trimOffspring", {"start": v(57, 60.41) * mm, "end": v(57, 41.5) * mm});
            skLineSegment(sketch, "E204.trimOffspring", {"start": v(53.3, 60.41) * mm, "end": v(53.3, 58.75) * mm});
            skLineSegment(sketch, "E205.trimOffspring", {"start": v(55.7, 62.59) * mm, "end": v(57, 62.59) * mm});
            skLineSegment(sketch, "E206.MirrorCS", {"start": v(-52, 62.59) * mm, "end": v(-53.3, 62.59) * mm});
            skLineSegment(sketch, "E207.MirrorCS", {"start": v(-55.7, 60.41) * mm, "end": v(-57, 60.41) * mm});
            skLineSegment(sketch, "E208.MirrorCS", {"start": v(-52, 60.41) * mm, "end": v(-53.3, 60.41) * mm});
            skLineSegment(sketch, "E209.MirrorCS", {"start": v(-55.7, 62.59) * mm, "end": v(-57, 62.59) * mm});
            skPoint(sketch, "E210.MirrorP", {"position": v(-54.5, 61.5) * mm});
            skLineSegment(sketch, "E211.MirrorCS", {"start": v(-52, 62.59) * mm, "end": v(-52, 60.41) * mm});
            skLineSegment(sketch, "E212.MirrorCS", {"start": v(-55.7, 60.41) * mm, "end": v(-55.7, 58.75) * mm});
            skLineSegment(sketch, "E213.MirrorCS", {"start": v(-53.3, 64.25) * mm, "end": v(-53.3, 62.59) * mm});
            skLineSegment(sketch, "E214.MirrorCS", {"start": v(-53.3, 60.41) * mm, "end": v(-53.3, 58.75) * mm});
            skLineSegment(sketch, "E215.MirrorCS", {"start": v(-55.7, 64.25) * mm, "end": v(-53.3, 64.25) * mm});
            skLineSegment(sketch, "E216.MirrorCS", {"start": v(-55.7, 58.75) * mm, "end": v(-53.3, 58.75) * mm});
            skLineSegment(sketch, "E217.MirrorCS", {"start": v(-55.7, 64.25) * mm, "end": v(-55.7, 62.59) * mm});
            skLineSegment(sketch, "E218.trimOffspring", {"start": v(-57, 60.41) * mm, "end": v(-57, -11.2) * mm, "construction": true});
            skLineSegment(sketch, "E219.trimOffspring", {"start": v(-57, 60.41) * mm, "end": v(-57, 41.5) * mm});
            skPoint(sketch, "E220.orphan", {"position": v(-57, 61.5) * mm});
            skPoint(sketch, "E221.MirrorCS.end.orphan", {"position": v(-52, 61.5) * mm});
            skPoint(sketch, "E222.orphan", {"position": v(52, 61.5) * mm});
            skPoint(sketch, "E223.start.orphan", {"position": v(57, 61.5) * mm});
            skPoint(sketch, "E224.center.orphan", {"position": v(-30, 121.5) * mm});
            skSolve(sketch);
        }
        {
            var Q0;
            Q0=makeQuery(id+"F6.imprint","IMPRINT",FACE,{"disambiguationData":[TD([[makeQuery(id+"F6.imprint","IMPRINT",EDGE,{"derivedFrom":sQuery(id+"F6.wireOp",EDGE,"E158.bottom")}),-1.0]])]});
            extrude(context, id + "F7", {"entities" : qUnion([Q0]), "oppositeDirection" : true, "depth" : 3 * mm, "offsetDistance" : 25 * mm});
        }
        {
            var Q0;
            Q0=makeQuery(id+"F7.opExtrude","CAP_FACE",FACE,{"disambiguationData":[OSD([sQuery(id+"F6.wireOp",EDGE,"E158.bottom"),sQuery(id+"F6.wireOp",EDGE,"E158.top"),sQuery(id+"F6.wireOp",EDGE,"E158.left"),sQuery(id+"F6.wireOp",EDGE,"E158.right"),sQuery(id+"F6.wireOp",EDGE,"E162.top"),sQuery(id+"F6.wireOp",EDGE,"E162.left"),sQuery(id+"F6.wireOp",EDGE,"E162.right"),sQuery(id+"F6.wireOp",EDGE,"E164.trimOffspring"),sQuery(id+"F6.wireOp",EDGE,"E166.MirrorCS"),sQuery(id+"F6.wireOp",EDGE,"E167.MirrorCS"),sQuery(id+"F6.wireOp",EDGE,"E168.MirrorCS"),sQuery(id+"F6.wireOp",EDGE,"E169.MirrorCS"),sQuery(id+"F6.wireOp",EDGE,"E170.MirrorCS"),sQuery(id+"F6.wireOp",EDGE,"E171.MirrorCS"),sQuery(id+"F6.wireOp",EDGE,"E172.MirrorCS"),sQuery(id+"F6.wireOp",EDGE,"E173.MirrorCS"),sQuery(id+"F6.wireOp",EDGE,"E174.MirrorCS"),sQuery(id+"F6.wireOp",EDGE,"E179.trimOffspring"),sQuery(id+"F6.wireOp",EDGE,"E183.trimOffspring"),sQuery(id+"F6.wireOp",EDGE,"E186.trimOffspring"),sQuery(id+"F6.wireOp",EDGE,"E189"),sQuery(id+"F6.wireOp",EDGE,"E190"),sQuery(id+"F6.wireOp",EDGE,"E191"),sQuery(id+"F6.wireOp",EDGE,"E192.trimOffspring"),sQuery(id+"F6.wireOp",EDGE,"E193.MirrorCS"),sQuery(id+"F6.wireOp",EDGE,"E194.MirrorCS"),sQuery(id+"F6.wireOp",EDGE,"E195.MirrorCS"),sQuery(id+"F6.wireOp",EDGE,"E197.trimOffspring"),sQuery(id+"F6.wireOp",EDGE,"E198.bottom"),sQuery(id+"F6.wireOp",EDGE,"E198.top"),sQuery(id+"F6.wireOp",EDGE,"E198.left"),sQuery(id+"F6.wireOp",EDGE,"E198.right"),sQuery(id+"F6.wireOp",EDGE,"E199.bottom"),sQuery(id+"F6.wireOp",EDGE,"E199.top"),sQuery(id+"F6.wireOp",EDGE,"E199.left"),sQuery(id+"F6.wireOp",EDGE,"E200.trimOffspring"),sQuery(id+"F6.wireOp",EDGE,"E201.trimOffspring"),sQuery(id+"F6.wireOp",EDGE,"E203.trimOffspring"),sQuery(id+"F6.wireOp",EDGE,"E204.trimOffspring"),sQuery(id+"F6.wireOp",EDGE,"E205.trimOffspring"),sQuery(id+"F6.wireOp",EDGE,"E206.MirrorCS"),sQuery(id+"F6.wireOp",EDGE,"E207.MirrorCS"),sQuery(id+"F6.wireOp",EDGE,"E208.MirrorCS"),sQuery(id+"F6.wireOp",EDGE,"E209.MirrorCS"),sQuery(id+"F6.wireOp",EDGE,"E211.MirrorCS"),sQuery(id+"F6.wireOp",EDGE,"E212.MirrorCS"),sQuery(id+"F6.wireOp",EDGE,"E213.MirrorCS"),sQuery(id+"F6.wireOp",EDGE,"E214.MirrorCS"),sQuery(id+"F6.wireOp",EDGE,"E215.MirrorCS"),sQuery(id+"F6.wireOp",EDGE,"E216.MirrorCS"),sQuery(id+"F6.wireOp",EDGE,"E217.MirrorCS"),sQuery(id+"F6.wireOp",EDGE,"E219.trimOffspring")])],"isStart":true});
            var sketch = newSketch(context, id + "F8", { "sketchPlane" : qUnion([Q0])});
            skLineSegment(sketch, "E225", {"start": v(-40, 120) * mm, "end": v(-20, 120) * mm, "construction": true});
            skLineSegment(sketch, "E226", {"start": v(-30, 120) * mm, "end": v(-30, 123) * mm, "construction": true});
            skCircle(sketch, "E227", {"center": v(-30, 121.5) * mm, "radius": 1.48 * mm});
            skCircle(sketch, "E228.MirrorC", {"center": v(30, 121.5) * mm, "radius": 1.48 * mm});
            skLineSegment(sketch, "E229", {"start": v(-52, 61.5) * mm, "end": v(52, 61.5) * mm, "construction": true});
            skCircle(sketch, "E230.MirrorC", {"center": v(-30, 1.5) * mm, "radius": 1.48 * mm});
            skCircle(sketch, "E231.MirrorC", {"center": v(30, 1.5) * mm, "radius": 1.48 * mm});
            skSolve(sketch);
        }
        {
            var Q0;
            Q0=makeQuery(id+"F8.imprint","IMPRINT",FACE,{"disambiguationData":[TD([[makeQuery(id+"F8.imprint","IMPRINT",EDGE,{"derivedFrom":sQuery(id+"F8.wireOp",EDGE,"E227")}),1.0]])]});
            var Q1;
            Q1=makeQuery(id+"F8.imprint","IMPRINT",FACE,{"disambiguationData":[TD([[makeQuery(id+"F8.imprint","IMPRINT",EDGE,{"derivedFrom":sQuery(id+"F8.wireOp",EDGE,"E228.MirrorC")}),-1.0]])]});
            var Q2;
            Q2=makeQuery(id+"F8.imprint","IMPRINT",FACE,{"disambiguationData":[TD([[makeQuery(id+"F8.imprint","IMPRINT",EDGE,{"derivedFrom":sQuery(id+"F8.wireOp",EDGE,"E230.MirrorC")}),-1.0]])]});
            var Q3;
            Q3=makeQuery(id+"F8.imprint","IMPRINT",FACE,{"disambiguationData":[TD([[makeQuery(id+"F8.imprint","IMPRINT",EDGE,{"derivedFrom":sQuery(id+"F8.wireOp",EDGE,"E231.MirrorC")}),1.0]])]});
            extrude(context, id + "F9", {"entities" : qUnion([Q0, Q1, Q2, Q3]), "operationType" : NewBodyOperationType.REMOVE, "endBound" : BoundingType.THROUGH_ALL, "oppositeDirection" : true, "depth" : 25 * mm, "offsetDistance" : 25 * mm});
        }
        {
            var Q0;
            Q0=makeQuery(id+"F7.opExtrude","SWEPT_BODY",BODY,{"disambiguationData":[OSD([sQuery(id+"F6.wireOp",EDGE,"E158.bottom"),sQuery(id+"F6.wireOp",EDGE,"E158.top"),sQuery(id+"F6.wireOp",EDGE,"E158.left"),sQuery(id+"F6.wireOp",EDGE,"E158.right"),sQuery(id+"F6.wireOp",EDGE,"E162.top"),sQuery(id+"F6.wireOp",EDGE,"E162.left"),sQuery(id+"F6.wireOp",EDGE,"E162.right"),sQuery(id+"F6.wireOp",EDGE,"E164.trimOffspring"),sQuery(id+"F6.wireOp",EDGE,"E166.MirrorCS"),sQuery(id+"F6.wireOp",EDGE,"E167.MirrorCS"),sQuery(id+"F6.wireOp",EDGE,"E168.MirrorCS"),sQuery(id+"F6.wireOp",EDGE,"E169.MirrorCS"),sQuery(id+"F6.wireOp",EDGE,"E170.MirrorCS"),sQuery(id+"F6.wireOp",EDGE,"E171.MirrorCS"),sQuery(id+"F6.wireOp",EDGE,"E172.MirrorCS"),sQuery(id+"F6.wireOp",EDGE,"E173.MirrorCS"),sQuery(id+"F6.wireOp",EDGE,"E174.MirrorCS"),sQuery(id+"F6.wireOp",EDGE,"E179.trimOffspring"),sQuery(id+"F6.wireOp",EDGE,"E183.trimOffspring"),sQuery(id+"F6.wireOp",EDGE,"E186.trimOffspring"),sQuery(id+"F6.wireOp",EDGE,"E189"),sQuery(id+"F6.wireOp",EDGE,"E190"),sQuery(id+"F6.wireOp",EDGE,"E191"),sQuery(id+"F6.wireOp",EDGE,"E192.trimOffspring"),sQuery(id+"F6.wireOp",EDGE,"E193.MirrorCS"),sQuery(id+"F6.wireOp",EDGE,"E194.MirrorCS"),sQuery(id+"F6.wireOp",EDGE,"E195.MirrorCS"),sQuery(id+"F6.wireOp",EDGE,"E197.trimOffspring"),sQuery(id+"F6.wireOp",EDGE,"E198.bottom"),sQuery(id+"F6.wireOp",EDGE,"E198.top"),sQuery(id+"F6.wireOp",EDGE,"E198.left"),sQuery(id+"F6.wireOp",EDGE,"E198.right"),sQuery(id+"F6.wireOp",EDGE,"E199.bottom"),sQuery(id+"F6.wireOp",EDGE,"E199.top"),sQuery(id+"F6.wireOp",EDGE,"E199.left"),sQuery(id+"F6.wireOp",EDGE,"E200.trimOffspring"),sQuery(id+"F6.wireOp",EDGE,"E201.trimOffspring"),sQuery(id+"F6.wireOp",EDGE,"E203.trimOffspring"),sQuery(id+"F6.wireOp",EDGE,"E204.trimOffspring"),sQuery(id+"F6.wireOp",EDGE,"E205.trimOffspring"),sQuery(id+"F6.wireOp",EDGE,"E206.MirrorCS"),sQuery(id+"F6.wireOp",EDGE,"E207.MirrorCS"),sQuery(id+"F6.wireOp",EDGE,"E208.MirrorCS"),sQuery(id+"F6.wireOp",EDGE,"E209.MirrorCS"),sQuery(id+"F6.wireOp",EDGE,"E211.MirrorCS"),sQuery(id+"F6.wireOp",EDGE,"E212.MirrorCS"),sQuery(id+"F6.wireOp",EDGE,"E213.MirrorCS"),sQuery(id+"F6.wireOp",EDGE,"E214.MirrorCS"),sQuery(id+"F6.wireOp",EDGE,"E215.MirrorCS"),sQuery(id+"F6.wireOp",EDGE,"E216.MirrorCS"),sQuery(id+"F6.wireOp",EDGE,"E217.MirrorCS"),sQuery(id+"F6.wireOp",EDGE,"E219.trimOffspring")])]});
            transform(context, id + "F10", {"entities" : qUnion([Q0]), "transformType" : TransformType.TRANSLATION_3D, "dx" : -117 * mm, "dy" : 0 * mm, "dz" : 0 * mm, "makeCopy" : true});
        }
        {
            var Q0;
            Q0=qCreatedBy(makeId("Front.planeOp"),FACE);
            cPlane(context, id + "F11", {"entities" : qUnion([Q0]), "cplaneType" : CPlaneType.OFFSET, "offset" : 60 * mm, "oppositeDirection" : true, "width" : 150 * mm, "height" : 150 * mm});
        }
        {
            var Q0;
            Q0=qCreatedBy(id+"F11.planeOp",FACE);
            var sketch = newSketch(context, id + "F12", { "sketchPlane" : qUnion([Q0])});
            skLineSegment(sketch, "E232", {"start": v(117.68, 0) * mm, "end": v(-119.27, 0) * mm, "construction": true});
            skLineSegment(sketch, "E233", {"start": v(0, 0) * mm, "end": v(0, 120) * mm, "construction": true});
            skLineSegment(sketch, "E234", {"start": v(57, 120) * mm, "end": v(40, 120) * mm, "construction": true});
            skLineSegment(sketch, "E235", {"start": v(102, 3) * mm, "end": v(40, 3) * mm, "construction": true});
            skLineSegment(sketch, "E236", {"start": v(57, 120) * mm, "end": v(57, 81.5) * mm, "construction": true});
            skLineSegment(sketch, "E237", {"start": v(57, -21.63) * mm, "end": v(-57, -21.63) * mm, "construction": true});
            skLineSegment(sketch, "E238", {"start": v(-57, -21.63) * mm, "end": v(-57, 120) * mm, "construction": true});
            skLineSegment(sketch, "E239.bottom", {"start": v(57, 120) * mm, "end": v(40, 120) * mm});
            skLineSegment(sketch, "E239.top", {"start": v(57, 3) * mm, "end": v(40, 3) * mm});
            skLineSegment(sketch, "E239.left", {"start": v(57, 120) * mm, "end": v(57, 81.5) * mm});
            skLineSegment(sketch, "E239.right", {"start": v(-57, 120) * mm, "end": v(-57, 3) * mm});
            skLineSegment(sketch, "E240", {"start": v(40, 120) * mm, "end": v(40, 123) * mm});
            skLineSegment(sketch, "E241", {"start": v(40, 123) * mm, "end": v(20, 123) * mm});
            skLineSegment(sketch, "E242", {"start": v(20, 123) * mm, "end": v(20, 120) * mm});
            skLineSegment(sketch, "E243.trimOffspring", {"start": v(20, 120) * mm, "end": v(-20, 120) * mm, "construction": true});
            skLineSegment(sketch, "E244.trimOffspring", {"start": v(20, 120) * mm, "end": v(-20, 120) * mm});
            skLineSegment(sketch, "E245", {"start": v(40, 121.5) * mm, "end": v(20, 121.5) * mm, "construction": true});
            skCircle(sketch, "E246", {"center": v(30, 121.5) * mm, "radius": 1.48 * mm});
            skLineSegment(sketch, "E247.MirrorCS", {"start": v(-20, 123) * mm, "end": v(-20, 120) * mm});
            skLineSegment(sketch, "E248.MirrorCS", {"start": v(-40, 120) * mm, "end": v(-40, 123) * mm});
            skLineSegment(sketch, "E249.MirrorCS", {"start": v(-40, 123) * mm, "end": v(-20, 123) * mm});
            skCircle(sketch, "E250.MirrorC", {"center": v(-30, 121.5) * mm, "radius": 1.48 * mm});
            skLineSegment(sketch, "E251.MirrorCS", {"start": v(-40, 121.5) * mm, "end": v(-20, 121.5) * mm, "construction": true});
            skLineSegment(sketch, "E252", {"start": v(57, 61.5) * mm, "end": v(-57, 61.5) * mm, "construction": true});
            skLineSegment(sketch, "E253.MirrorCS", {"start": v(-20, 0) * mm, "end": v(-20, 3) * mm});
            skLineSegment(sketch, "E254.MirrorCS", {"start": v(40, 3) * mm, "end": v(40, 0) * mm});
            skLineSegment(sketch, "E255.MirrorCS", {"start": v(20, 0) * mm, "end": v(20, 3) * mm});
            skCircle(sketch, "E256.MirrorC", {"center": v(-30, 1.5) * mm, "radius": 1.48 * mm});
            skLineSegment(sketch, "E257.MirrorCS", {"start": v(-40, 3) * mm, "end": v(-40, 0) * mm});
            skCircle(sketch, "E258.MirrorC", {"center": v(30, 1.5) * mm, "radius": 1.48 * mm});
            skLineSegment(sketch, "E259.MirrorCS", {"start": v(40, 1.5) * mm, "end": v(20, 1.5) * mm, "construction": true});
            skLineSegment(sketch, "E260.MirrorCS", {"start": v(40, 0) * mm, "end": v(20, 0) * mm});
            skLineSegment(sketch, "E261.MirrorCS", {"start": v(-40, 1.5) * mm, "end": v(-20, 1.5) * mm, "construction": true});
            skLineSegment(sketch, "E262.MirrorCS", {"start": v(-40, 0) * mm, "end": v(-20, 0) * mm});
            skLineSegment(sketch, "E263.trimOffspring", {"start": v(-40, 120) * mm, "end": v(-57, 120) * mm, "construction": true});
            skLineSegment(sketch, "E264.trimOffspring", {"start": v(-40, 120) * mm, "end": v(-57, 120) * mm});
            skLineSegment(sketch, "E265.trimOffspring", {"start": v(-40, 3) * mm, "end": v(-167.8, 3) * mm, "construction": true});
            skLineSegment(sketch, "E266.trimOffspring", {"start": v(-40, 3) * mm, "end": v(-57, 3) * mm});
            skLineSegment(sketch, "E267.trimOffspring", {"start": v(20, 3) * mm, "end": v(-20, 3) * mm, "construction": true});
            skLineSegment(sketch, "E268.trimOffspring", {"start": v(20, 3) * mm, "end": v(-20, 3) * mm});
            skLineSegment(sketch, "E269", {"start": v(57, 81.5) * mm, "end": v(60, 81.5) * mm});
            skLineSegment(sketch, "E270", {"start": v(60, 41.5) * mm, "end": v(57, 41.5) * mm});
            skLineSegment(sketch, "E271", {"start": v(60, 41.5) * mm, "end": v(60, 81.5) * mm});
            skLineSegment(sketch, "E272.trimOffspring", {"start": v(57, 41.5) * mm, "end": v(57, -21.63) * mm, "construction": true});
            skLineSegment(sketch, "E273.trimOffspring", {"start": v(57, 41.5) * mm, "end": v(57, 3) * mm});
            skLineSegment(sketch, "E274", {"start": v(57, 61.5) * mm, "end": v(60, 61.5) * mm, "construction": true});
            skCircle(sketch, "E275", {"center": v(58.5, 61.5) * mm, "radius": 1.48 * mm});
            skLineSegment(sketch, "E276.MirrorCS", {"start": v(-60, 41.5) * mm, "end": v(-57, 41.5) * mm});
            skLineSegment(sketch, "E277.MirrorCS", {"start": v(-57, 81.5) * mm, "end": v(-60, 81.5) * mm});
            skLineSegment(sketch, "E278.MirrorCS", {"start": v(-57, 61.5) * mm, "end": v(-60, 61.5) * mm, "construction": true});
            skLineSegment(sketch, "E279.MirrorCS", {"start": v(-60, 41.5) * mm, "end": v(-60, 81.5) * mm});
            skCircle(sketch, "E280.MirrorC", {"center": v(-58.5, 61.5) * mm, "radius": 1.48 * mm});
            skSolve(sketch);
        }
        {
            var Q0;
            Q0=makeQuery(id+"F12.imprint","IMPRINT",FACE,{"disambiguationData":[TD([[makeQuery(id+"F12.imprint","IMPRINT",EDGE,{"derivedFrom":sQuery(id+"F12.wireOp",EDGE,"E239.bottom")}),1.0]])]});
            var Q1;
            {var subQ1=sQuery(id+"F12.wireOp",EDGE,"E276.MirrorCS");Q1=makeQuery(id+"F12.imprint","IMPRINT",FACE,{"disambiguationData":[TD([[makeQuery(id+"F12.imprint","IMPRINT",EDGE,{"derivedFrom":subQ1}),1.0]])]});}
            extrude(context, id + "F13", {"entities" : qUnion([Q0, Q1]), "depth" : 3 * mm, "offsetDistance" : 25 * mm});
        }
        {
            var Q0;
            Q0=makeQuery(id+"F13.opExtrude","SWEPT_BODY",BODY,{"disambiguationData":[OSD([sQuery(id+"F12.wireOp",EDGE,"E239.bottom"),sQuery(id+"F12.wireOp",EDGE,"E239.top"),sQuery(id+"F12.wireOp",EDGE,"E239.left"),sQuery(id+"F12.wireOp",EDGE,"E239.right"),sQuery(id+"F12.wireOp",EDGE,"E240"),sQuery(id+"F12.wireOp",EDGE,"E241"),sQuery(id+"F12.wireOp",EDGE,"E242"),sQuery(id+"F12.wireOp",EDGE,"E244.trimOffspring"),sQuery(id+"F12.wireOp",EDGE,"E246"),sQuery(id+"F12.wireOp",EDGE,"E247.MirrorCS"),sQuery(id+"F12.wireOp",EDGE,"E248.MirrorCS"),sQuery(id+"F12.wireOp",EDGE,"E249.MirrorCS"),sQuery(id+"F12.wireOp",EDGE,"E250.MirrorC"),sQuery(id+"F12.wireOp",EDGE,"E253.MirrorCS"),sQuery(id+"F12.wireOp",EDGE,"E254.MirrorCS"),sQuery(id+"F12.wireOp",EDGE,"E255.MirrorCS"),sQuery(id+"F12.wireOp",EDGE,"E256.MirrorC"),sQuery(id+"F12.wireOp",EDGE,"E257.MirrorCS"),sQuery(id+"F12.wireOp",EDGE,"E258.MirrorC"),sQuery(id+"F12.wireOp",EDGE,"E260.MirrorCS"),sQuery(id+"F12.wireOp",EDGE,"E262.MirrorCS"),sQuery(id+"F12.wireOp",EDGE,"E264.trimOffspring"),sQuery(id+"F12.wireOp",EDGE,"E266.trimOffspring"),sQuery(id+"F12.wireOp",EDGE,"E268.trimOffspring"),sQuery(id+"F12.wireOp",EDGE,"E269"),sQuery(id+"F12.wireOp",EDGE,"E270"),sQuery(id+"F12.wireOp",EDGE,"E271"),sQuery(id+"F12.wireOp",EDGE,"E273.trimOffspring"),sQuery(id+"F12.wireOp",EDGE,"E275"),sQuery(id+"F12.wireOp",EDGE,"E276.MirrorCS"),sQuery(id+"F12.wireOp",EDGE,"E277.MirrorCS"),sQuery(id+"F12.wireOp",EDGE,"E279.MirrorCS"),sQuery(id+"F12.wireOp",EDGE,"E280.MirrorC")])]});
            transform(context, id + "F14", {"entities" : qUnion([Q0]), "transformType" : TransformType.TRANSLATION_3D, "dx" : 0 * mm, "dy" : -117 * mm, "dz" : 0 * mm, "makeCopy" : true});
        }
        {
            var Q0;
            Q0=makeQuery(id+"F14.opPattern","COPY",FACE,{"derivedFrom":makeQuery(id+"F13.opExtrude","CAP_FACE",FACE,{"disambiguationData":[OSD([sQuery(id+"F12.wireOp",EDGE,"E239.bottom"),sQuery(id+"F12.wireOp",EDGE,"E239.top"),sQuery(id+"F12.wireOp",EDGE,"E239.left"),sQuery(id+"F12.wireOp",EDGE,"E239.right"),sQuery(id+"F12.wireOp",EDGE,"E240"),sQuery(id+"F12.wireOp",EDGE,"E241"),sQuery(id+"F12.wireOp",EDGE,"E242"),sQuery(id+"F12.wireOp",EDGE,"E244.trimOffspring"),sQuery(id+"F12.wireOp",EDGE,"E246"),sQuery(id+"F12.wireOp",EDGE,"E247.MirrorCS"),sQuery(id+"F12.wireOp",EDGE,"E248.MirrorCS"),sQuery(id+"F12.wireOp",EDGE,"E249.MirrorCS"),sQuery(id+"F12.wireOp",EDGE,"E250.MirrorC"),sQuery(id+"F12.wireOp",EDGE,"E253.MirrorCS"),sQuery(id+"F12.wireOp",EDGE,"E254.MirrorCS"),sQuery(id+"F12.wireOp",EDGE,"E255.MirrorCS"),sQuery(id+"F12.wireOp",EDGE,"E256.MirrorC"),sQuery(id+"F12.wireOp",EDGE,"E257.MirrorCS"),sQuery(id+"F12.wireOp",EDGE,"E258.MirrorC"),sQuery(id+"F12.wireOp",EDGE,"E260.MirrorCS"),sQuery(id+"F12.wireOp",EDGE,"E262.MirrorCS"),sQuery(id+"F12.wireOp",EDGE,"E264.trimOffspring"),sQuery(id+"F12.wireOp",EDGE,"E266.trimOffspring"),sQuery(id+"F12.wireOp",EDGE,"E268.trimOffspring"),sQuery(id+"F12.wireOp",EDGE,"E269"),sQuery(id+"F12.wireOp",EDGE,"E270"),sQuery(id+"F12.wireOp",EDGE,"E271"),sQuery(id+"F12.wireOp",EDGE,"E273.trimOffspring"),sQuery(id+"F12.wireOp",EDGE,"E275"),sQuery(id+"F12.wireOp",EDGE,"E276.MirrorCS"),sQuery(id+"F12.wireOp",EDGE,"E277.MirrorCS"),sQuery(id+"F12.wireOp",EDGE,"E279.MirrorCS"),sQuery(id+"F12.wireOp",EDGE,"E280.MirrorC")])],"isStart":false}),"instanceName":"1"});
            var sketch = newSketch(context, id + "F15", { "sketchPlane" : qUnion([Q0])});
            skLineSegment(sketch, "E281", {"start": v(-85.05, 86.16) * mm, "end": v(91.93, 86.16) * mm, "construction": true});
            skCircle(sketch, "E282", {"center": v(26.12, 86.16) * mm, "radius": 10 * mm});
            skCircle(sketch, "E283.MirrorC", {"center": v(-26.12, 86.16) * mm, "radius": 10 * mm});
            skLineSegment(sketch, "E284", {"start": v(99.39, 52.36) * mm, "end": v(99.39, 27.74) * mm, "construction": true});
            skLineSegment(sketch, "E285", {"start": v(99.39, 27.74) * mm, "end": v(-94.64, 27.74) * mm, "construction": true});
            skArc(sketch, "E286", {"start": v(-26.12, 52.36) * mm, "mid": v(0, 45.26) * mm, "end": v(26.12, 52.36) * mm});
            skArc(sketch, "E287", {"start": v(-26.12, 52.36) * mm, "mid": v(0, 32.38) * mm, "end": v(26.12, 52.36) * mm});
            skSolve(sketch);
        }
        {
            var Q0;
            Q0=makeQuery(id+"F15.imprint","IMPRINT",FACE,{"disambiguationData":[TD([[makeQuery(id+"F15.imprint","IMPRINT",EDGE,{"derivedFrom":sQuery(id+"F15.wireOp",EDGE,"E282")}),1.0]])]});
            var Q1;
            Q1=makeQuery(id+"F15.imprint","IMPRINT",FACE,{"disambiguationData":[TD([[makeQuery(id+"F15.imprint","IMPRINT",EDGE,{"derivedFrom":sQuery(id+"F15.wireOp",EDGE,"E286")}),-1.0]])]});
            var Q2;
            Q2=makeQuery(id+"F15.imprint","IMPRINT",FACE,{"disambiguationData":[TD([[makeQuery(id+"F15.imprint","IMPRINT",EDGE,{"derivedFrom":sQuery(id+"F15.wireOp",EDGE,"E283.MirrorC")}),-1.0]])]});
            extrude(context, id + "F16", {"entities" : qUnion([Q0, Q1, Q2]), "operationType" : NewBodyOperationType.REMOVE, "oppositeDirection" : true, "depth" : 25 * mm, "offsetDistance" : 25 * mm});
        }
        {
            var Q0;
            Q0=makeQuery(id+"F3.imprint","IMPRINT",FACE,{"disambiguationData":[TD([[makeQuery(id+"F3.imprint","IMPRINT",EDGE,{"derivedFrom":makeQuery(id+"F2.opPattern","COPY",EDGE,{"derivedFrom":makeQuery(id+"F1.opExtrude","CAP_EDGE",EDGE,{"disambiguationData":[OSD([sQuery(id+"F0.wireOp",EDGE,"E148")])],"isStart":false}),"instanceName":"1"})}),1.0]])]});
            extrude(context, id + "F17", {"entities" : qUnion([Q0]), "operationType" : NewBodyOperationType.ADD, "oppositeDirection" : true, "depth" : 3 * mm, "offsetDistance" : 25 * mm});
        }
    });
